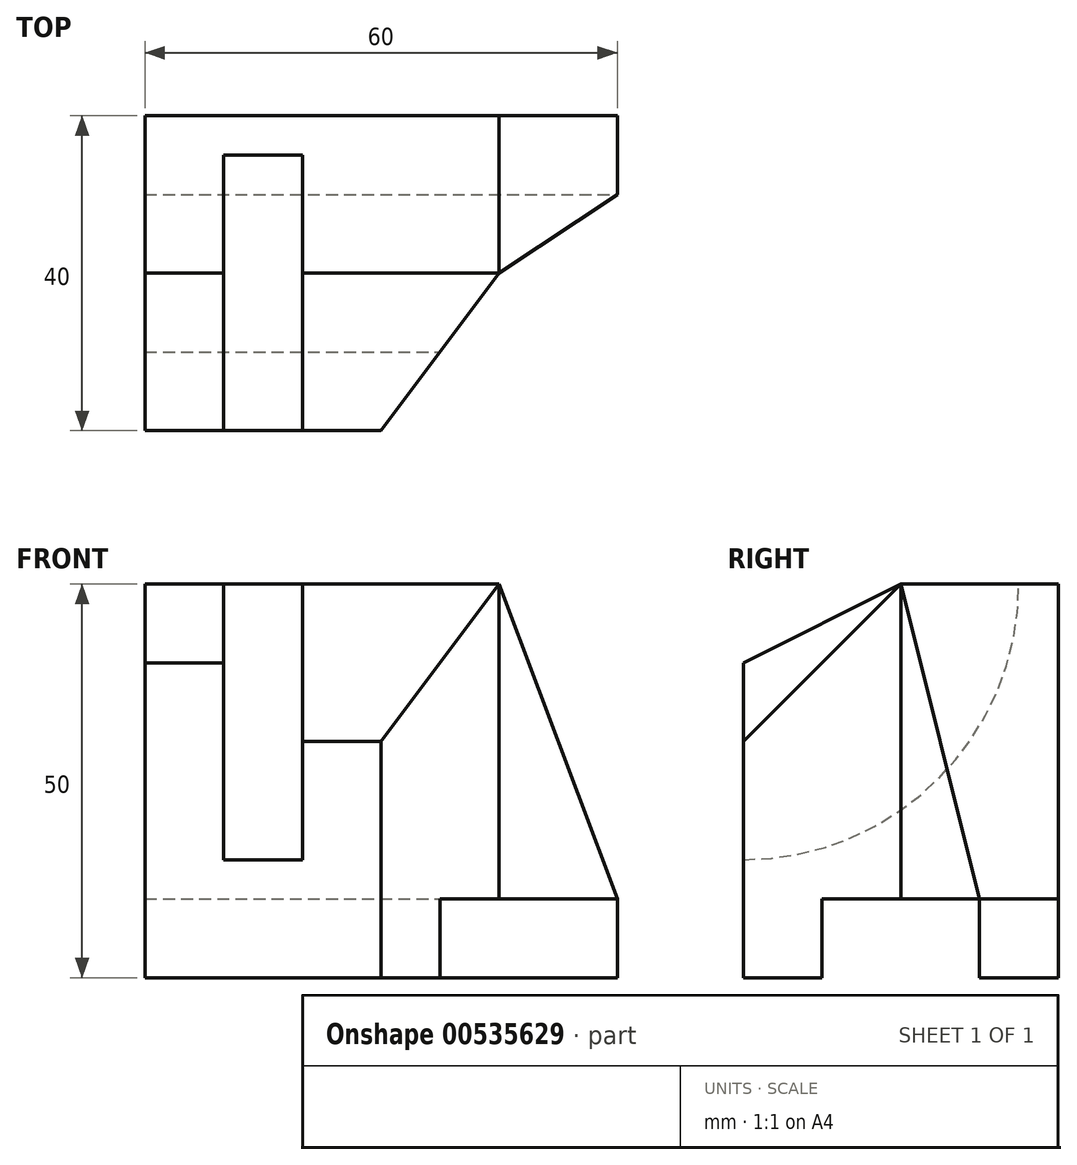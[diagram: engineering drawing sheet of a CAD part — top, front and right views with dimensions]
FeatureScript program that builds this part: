
annotation { "Feature Type Name" : "Feature", "Feature Type Description" : "" }
export const myFeature = defineFeature(function(context is Context, id is Id, definition is map)
    precondition{}
    {
        {
            var Q0;
            Q0=qCreatedBy(makeId("Front.planeOp"),FACE);
            var sketch = newSketch(context, id + "F0", { "sketchPlane" : qUnion([Q0])});
            skLineSegment(sketch, "E0.bottom", {"start": v(0, 0) * mm, "end": v(60, 0) * mm});
            skLineSegment(sketch, "E0.top", {"start": v(0, 50) * mm, "end": v(60, 50) * mm});
            skLineSegment(sketch, "E0.left", {"start": v(0, 0) * mm, "end": v(0, 50) * mm});
            skLineSegment(sketch, "E0.right", {"start": v(60, 0) * mm, "end": v(60, 50) * mm});
            skSolve(sketch);
        }
        {
            var Q0;
            Q0=makeQuery(id+"F0.imprint","IMPRINT",FACE,{"disambiguationData":[TD([[makeQuery(id+"F0.imprint","IMPRINT",EDGE,{"derivedFrom":sQuery(id+"F0.wireOp",EDGE,"E0.bottom")}),1.0]])]});
            extrude(context, id + "F1", {"entities" : qUnion([Q0]), "depth" : 40 * mm, "offsetDistance" : 25 * mm});
        }
        {
            var Q0;
            Q0=makeQuery(id+"F1.opExtrude","SWEPT_FACE",FACE,{"disambiguationData":[OSD([sQuery(id+"F0.wireOp",EDGE,"E0.right")])]});
            var sketch = newSketch(context, id + "F2", { "sketchPlane" : qUnion([Q0])});
            skLineSegment(sketch, "E1", {"start": v(-40, 0) * mm, "end": v(-30, 0) * mm});
            skLineSegment(sketch, "E2.bottom", {"start": v(-30, 0) * mm, "end": v(-10, 0) * mm});
            skLineSegment(sketch, "E2.top", {"start": v(-30, 10) * mm, "end": v(-10, 10) * mm});
            skLineSegment(sketch, "E2.left", {"start": v(-30, 0) * mm, "end": v(-30, 10) * mm});
            skLineSegment(sketch, "E2.right", {"start": v(-10, 0) * mm, "end": v(-10, 10) * mm});
            skSolve(sketch);
        }
        {
            var Q0;
            Q0 = qSketchRegion(id + "F2", true);
            extrude(context, id + "F3", {"entities" : qUnion([Q0]), "operationType" : NewBodyOperationType.REMOVE, "oppositeDirection" : true, "depth" : 60 * mm, "offsetDistance" : 25 * mm});
        }
        {
            var Q0;
            Q0=makeQuery(id+"F1.opExtrude","SWEPT_FACE",FACE,{"disambiguationData":[OSD([sQuery(id+"F0.wireOp",EDGE,"E0.top")])]});
            var sketch = newSketch(context, id + "F4", { "sketchPlane" : qUnion([Q0])});
            skLineSegment(sketch, "E3.bottom", {"start": v(60, -40) * mm, "end": v(45, -40) * mm});
            skLineSegment(sketch, "E3.top", {"start": v(60, -20) * mm, "end": v(45, -20) * mm});
            skLineSegment(sketch, "E3.left", {"start": v(60, -40) * mm, "end": v(60, -20) * mm});
            skLineSegment(sketch, "E3.right", {"start": v(45, -40) * mm, "end": v(45, -20) * mm});
            skSolve(sketch);
        }
        {
            var Q0;
            Q0=makeQuery(id+"F4.imprint","IMPRINT",FACE,{"disambiguationData":[TD([[makeQuery(id+"F4.imprint","IMPRINT",EDGE,{"derivedFrom":sQuery(id+"F4.wireOp",EDGE,"E3.bottom")}),1.0]])]});
            extrude(context, id + "F5", {"entities" : qUnion([Q0]), "operationType" : NewBodyOperationType.REMOVE, "oppositeDirection" : true, "depth" : 50 * mm, "offsetDistance" : 25 * mm});
        }
        {
            var Q0;
            Q0=makeQuery(id+"F1.opExtrude","SWEPT_FACE",FACE,{"disambiguationData":[OSD([sQuery(id+"F0.wireOp",EDGE,"E0.top")])]});
            var sketch = newSketch(context, id + "F6", { "sketchPlane" : qUnion([Q0])});
            skLineSegment(sketch, "E4", {"start": v(60, -20) * mm, "end": v(60, -10) * mm});
            skLineSegment(sketch, "E5", {"start": v(60, -10) * mm, "end": v(45, -20) * mm});
            skLineSegment(sketch, "E6", {"start": v(45, -40) * mm, "end": v(45, -20) * mm});
            skLineSegment(sketch, "E7", {"start": v(45, -20) * mm, "end": v(30, -40) * mm});
            skLineSegment(sketch, "E8", {"start": v(30, -40) * mm, "end": v(45, -40) * mm});
            skLineSegment(sketch, "E9", {"start": v(60, 0) * mm, "end": v(45, 0) * mm});
            skLineSegment(sketch, "E10", {"start": v(45, -20) * mm, "end": v(20, -20) * mm});
            skLineSegment(sketch, "E11", {"start": v(20, -20) * mm, "end": v(20, -40) * mm});
            skLineSegment(sketch, "E12", {"start": v(20, -40) * mm, "end": v(30, -40) * mm});
            skLineSegment(sketch, "E13", {"start": v(45, 0) * mm, "end": v(45, -20) * mm});
            skLineSegment(sketch, "E14.bottom", {"start": v(20, -40) * mm, "end": v(10, -40) * mm});
            skLineSegment(sketch, "E14.top", {"start": v(20, -5) * mm, "end": v(10, -5) * mm});
            skLineSegment(sketch, "E14.left", {"start": v(20, -40) * mm, "end": v(20, -5) * mm});
            skLineSegment(sketch, "E14.right", {"start": v(10, -40) * mm, "end": v(10, -5) * mm});
            skLineSegment(sketch, "E15.bottom", {"start": v(0, -40) * mm, "end": v(10, -40) * mm});
            skLineSegment(sketch, "E15.top", {"start": v(0, -20) * mm, "end": v(10, -20) * mm});
            skLineSegment(sketch, "E15.left", {"start": v(0, -40) * mm, "end": v(0, -20) * mm});
            skLineSegment(sketch, "E15.right", {"start": v(10, -40) * mm, "end": v(10, -20) * mm});
            skSolve(sketch);
        }
        {
            var Q0;
            Q0=makeQuery(id+"F6.imprint","IMPRINT",FACE,{"disambiguationData":[TD([[makeQuery(id+"F6.imprint","IMPRINT",EDGE,{"derivedFrom":sQuery(id+"F6.wireOp",EDGE,"E4")}),1.0]])]});
            var Q1;
            Q1=makeQuery(id+"F6.imprint","IMPRINT",FACE,{"disambiguationData":[TD([[makeQuery(id+"F6.imprint","IMPRINT",EDGE,{"derivedFrom":sQuery(id+"F6.wireOp",EDGE,"E6")}),1.0]])]});
            extrude(context, id + "F7", {"entities" : qUnion([Q0, Q1]), "operationType" : NewBodyOperationType.REMOVE, "oppositeDirection" : true, "depth" : 50 * mm, "offsetDistance" : 25 * mm});
        }
        {
            var Q0;
            Q0=makeQuery(id+"F1.opExtrude","SWEPT_FACE",FACE,{"disambiguationData":[OSD([sQuery(id+"F0.wireOp",EDGE,"E0.right")])]});
            var sketch = newSketch(context, id + "F8", { "sketchPlane" : qUnion([Q0])});
            skLineSegment(sketch, "E16", {"start": v(-10, 10) * mm, "end": v(0, 10) * mm});
            skSolve(sketch);
        }
        {
            var Q0;
            Q0=makeQuery(id+"F1.opExtrude","CAP_FACE",FACE,{"disambiguationData":[OSD([sQuery(id+"F0.wireOp",EDGE,"E0.bottom"),sQuery(id+"F0.wireOp",EDGE,"E0.top"),sQuery(id+"F0.wireOp",EDGE,"E0.left"),sQuery(id+"F0.wireOp",EDGE,"E0.right")])],"isStart":false});
            var sketch = newSketch(context, id + "F9", { "sketchPlane" : qUnion([Q0])});
            skLineSegment(sketch, "E17", {"start": v(30, 0) * mm, "end": v(30, 30) * mm});
            skLineSegment(sketch, "E18.bottom", {"start": v(0, 50) * mm, "end": v(10, 50) * mm});
            skLineSegment(sketch, "E18.top", {"start": v(0, 40) * mm, "end": v(10, 40) * mm});
            skLineSegment(sketch, "E18.left", {"start": v(0, 50) * mm, "end": v(0, 40) * mm});
            skLineSegment(sketch, "E18.right", {"start": v(10, 50) * mm, "end": v(10, 40) * mm});
            skSolve(sketch);
        }
        {
            var Q0;
            Q0=sQuery(id+"F6.wireOp",VERTEX,"E9.end");
            var Q1;
            Q1=sQuery(id+"F6.wireOp",VERTEX,"E7.start");
            var Q2;
            Q2=sQuery(id+"F8.wireOp",VERTEX,"E16.end");
            cPlane(context, id + "F10", {"entities" : qUnion([Q0, Q1, Q2]), "cplaneType" : CPlaneType.THREE_POINT, "offset" : 25 * mm, "width" : 150 * mm, "height" : 150 * mm});
        }
        {
            var Q0;
            {var subQ0=sQuery(id+"F6.wireOp",EDGE,"E5");Q0=makeQuery(id+"F6.imprint","IMPRINT",FACE,{"disambiguationData":[TD([[makeQuery(id+"F6.imprint","IMPRINT",EDGE,{"derivedFrom":subQ0}),-1.0]])]});}
            var Q1;
            Q1=qCreatedBy(id+"F10.planeOp",FACE);
            extrude(context, id + "F11", {"entities" : qUnion([Q0]), "operationType" : NewBodyOperationType.REMOVE, "endBound" : BoundingType.UP_TO_SURFACE, "oppositeDirection" : true, "depth" : 25 * mm, "endBoundEntityFace" : qUnion([Q1]), "offsetDistance" : 25 * mm});
        }
        {
            var Q0;
            Q0=sQuery(id+"F9.wireOp",VERTEX,"E17.end");
            var Q1;
            Q1=sQuery(id+"F6.wireOp",VERTEX,"E11.start");
            var Q2;
            Q2=sQuery(id+"F6.wireOp",VERTEX,"E7.start");
            cPlane(context, id + "F12", {"entities" : qUnion([Q0, Q1, Q2]), "cplaneType" : CPlaneType.THREE_POINT, "offset" : 25 * mm, "width" : 150 * mm, "height" : 150 * mm});
        }
        {
            var Q0;
            Q0=makeQuery(id+"F6.imprint","IMPRINT",FACE,{"disambiguationData":[TD([[makeQuery(id+"F6.imprint","IMPRINT",EDGE,{"derivedFrom":sQuery(id+"F6.wireOp",EDGE,"E7")}),-1.0]])]});
            var Q1;
            Q1=qCreatedBy(id+"F12.planeOp",FACE);
            extrude(context, id + "F13", {"entities" : qUnion([Q0]), "operationType" : NewBodyOperationType.REMOVE, "endBound" : BoundingType.UP_TO_SURFACE, "oppositeDirection" : true, "depth" : 25 * mm, "endBoundEntityFace" : qUnion([Q1]), "offsetDistance" : 25 * mm});
        }
        {
            var Q0;
            {var subQ3=sQuery(id+"F6.wireOp",EDGE,"E14.bottom");Q0=makeQuery(id+"F6.imprint","IMPRINT",FACE,{"disambiguationData":[TD([[makeQuery(id+"F6.imprint","IMPRINT",EDGE,{"derivedFrom":subQ3}),1.0]])]});}
            extrude(context, id + "F14", {"entities" : qUnion([Q0]), "operationType" : NewBodyOperationType.REMOVE, "oppositeDirection" : true, "depth" : 35 * mm, "offsetDistance" : 25 * mm});
        }
        {
            var Q0;
            Q0=makeQuery(id+"F14.boolean.opBoolean","COPY",EDGE,{"derivedFrom":makeQuery(id+"F14.opExtrude","CAP_EDGE",EDGE,{"disambiguationData":[OSD([sQuery(id+"F6.wireOp",EDGE,"E14.top")])],"isStart":false})});
            fillet(context, id + "F15", {"entities" : qUnion([Q0]), "radius" : 35 * mm, "tangentPropagation" : true, "allowEdgeOverflow" : false});
        }
        {
            var Q0;
            Q0=makeQuery(id+"F1.opExtrude","SWEPT_EDGE",EDGE,{"disambiguationData":[OSD([sQuery(id+"F0.wireOp",EDGE,"E0.top"),sQuery(id+"F0.wireOp",EDGE,"E0.left")])]});
            cPoint(context, id + "F16", {"entities" : qUnion([Q0]), "parameter" : 0.5});
        }
        {
            var Q0;
            Q0 = qCreatedBy(id + "F16" ,VERTEX);
            var Q1;
            Q1=sQuery(id+"F6.wireOp",VERTEX,"E15.top.end");
            var Q2;
            Q2=sQuery(id+"F9.wireOp",VERTEX,"E18.right.end");
            cPlane(context, id + "F17", {"entities" : qUnion([Q0, Q1, Q2]), "cplaneType" : CPlaneType.THREE_POINT, "offset" : 25 * mm, "width" : 150 * mm, "height" : 150 * mm});
        }
        {
            var Q0;
            Q0=makeQuery(id+"F9.imprint","IMPRINT",FACE,{"disambiguationData":[TD([[makeQuery(id+"F9.imprint","IMPRINT",EDGE,{"derivedFrom":sQuery(id+"F9.wireOp",EDGE,"E18.bottom")}),-1.0]])]});
            var Q1;
            Q1=qCreatedBy(id+"F17.planeOp",FACE);
            extrude(context, id + "F18", {"entities" : qUnion([Q0]), "operationType" : NewBodyOperationType.REMOVE, "endBound" : BoundingType.UP_TO_SURFACE, "oppositeDirection" : true, "depth" : 25 * mm, "endBoundEntityFace" : qUnion([Q1]), "offsetDistance" : 25 * mm});
        }
    });
